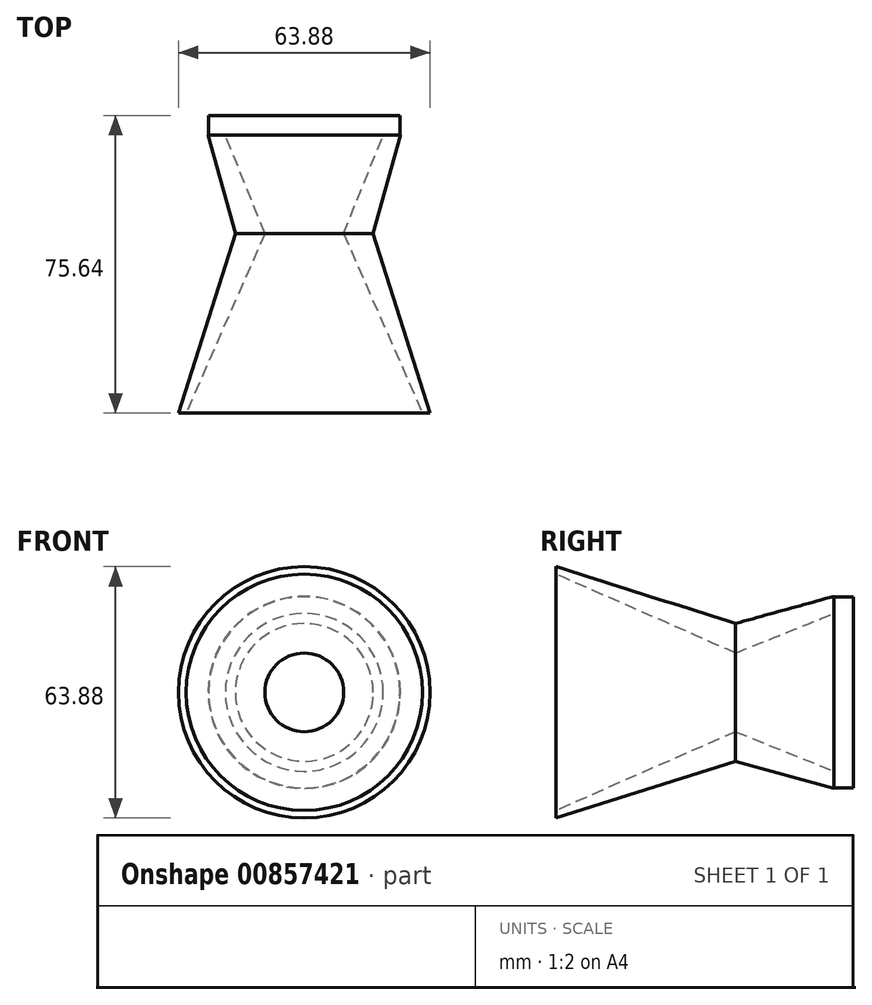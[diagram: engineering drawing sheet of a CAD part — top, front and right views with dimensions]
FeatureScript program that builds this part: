
annotation { "Feature Type Name" : "Feature", "Feature Type Description" : "" }
export const myFeature = defineFeature(function(context is Context, id is Id, definition is map)
    precondition{}
    {
        {
            var Q0;
            Q0=qCreatedBy(makeId("Right.planeOp"),FACE);
            var sketch = newSketch(context, id + "F0", { "sketchPlane" : qUnion([Q0])});
            skLineSegment(sketch, "E0", {"start": v(0, 0) * mm, "end": v(25, 0) * mm});
            skLineSegment(sketch, "E1", {"start": v(0, 0) * mm, "end": v(-26.4, 0) * mm});
            skLineSegment(sketch, "E2", {"start": v(25, 20.05) * mm, "end": v(0, 10) * mm});
            skLineSegment(sketch, "E3", {"start": v(-45.64, 30.03) * mm, "end": v(0, 10) * mm});
            skLineSegment(sketch, "E4", {"start": v(-45.64, 30.03) * mm, "end": v(-45.64, 31.94) * mm});
            skLineSegment(sketch, "E5", {"start": v(-45.64, 31.94) * mm, "end": v(0, 17.51) * mm});
            skLineSegment(sketch, "E6", {"start": v(0, 17.51) * mm, "end": v(25, 24.4) * mm});
            skLineSegment(sketch, "E7", {"start": v(25, 24.4) * mm, "end": v(25, 20.05) * mm});
            skSolve(sketch);
        }
        {
            var Q0;
            Q0 = qSketchRegion(id + "F0", true);
            var Q1;
            Q1=sQuery(id+"F0.wireOp",EDGE,"E1");
            revolve(context, id + "F1", {"surfaceOperationType" : NewSurfaceOperationType.NEW, "entities" : qUnion([Q0]), "axis" : qUnion([Q1]), "revolveType" : RevolveType.FULL});
        }
        {
            var Q0;
            Q0=makeQuery(id+"F1.opRevolve","SWEPT_FACE",FACE,{"disambiguationData":[OSD([sQuery(id+"F0.wireOp",EDGE,"E7")])]});
            var sketch = newSketch(context, id + "F2", { "sketchPlane" : qUnion([Q0])});
            skCircle(sketch, "E8", {"center": v(0, 0) * mm, "radius": 20.23 * mm});
            skSolve(sketch);
        }
        {
            var Q0;
            Q0=makeQuery(id+"F2.imprint","IMPRINT",FACE,{"disambiguationData":[TD([[makeQuery(id+"F2.imprint","IMPRINT",EDGE,{"derivedFrom":sQuery(id+"F2.wireOp",EDGE,"E8")}),-1.0]])]});
            var sketch = newSketch(context, id + "F3", { "sketchPlane" : qUnion([Q0])});
            skCircle(sketch, "E9", {"center": v(0, 0) * mm, "radius": 24.29 * mm});
            skSolve(sketch);
        }
        {
            var Q0;
            Q0 = qSketchRegion(id + "F3", true);
            extrude(context, id + "F4", {"entities" : qUnion([Q0]), "operationType" : NewBodyOperationType.ADD, "depth" : 5 * mm, "offsetDistance" : 25 * mm});
        }
    });
